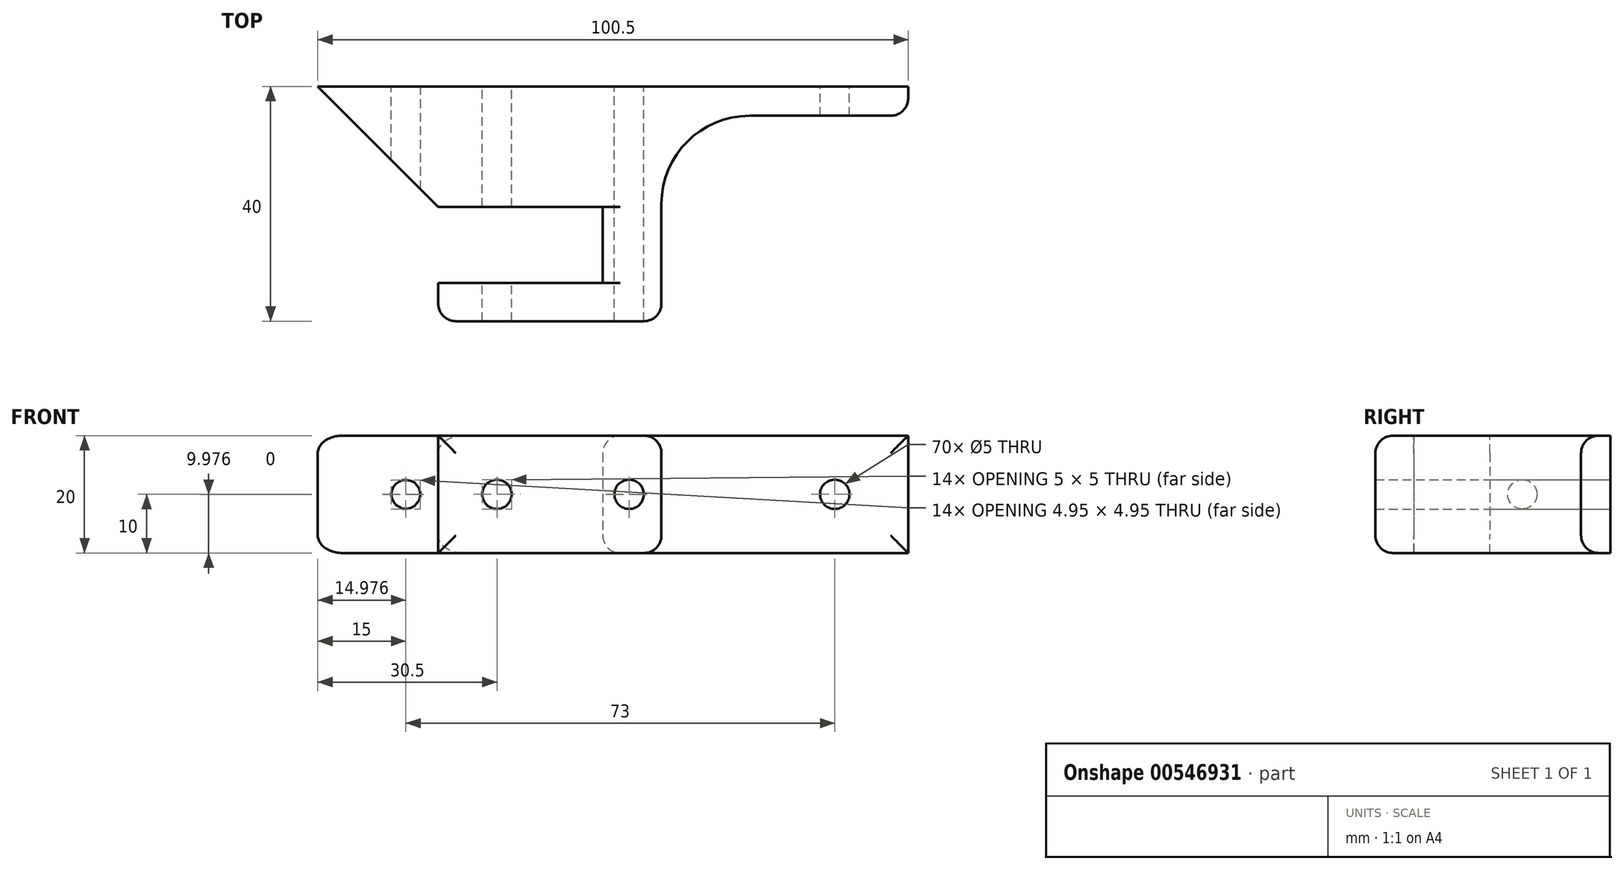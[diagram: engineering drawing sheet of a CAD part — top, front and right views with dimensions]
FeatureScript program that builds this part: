
annotation { "Feature Type Name" : "Feature", "Feature Type Description" : "" }
export const myFeature = defineFeature(function(context is Context, id is Id, definition is map)
    precondition{}
    {
        {
            var Q0;
            Q0=qCreatedBy(makeId("Top.planeOp"),FACE);
            var sketch = newSketch(context, id + "F0", { "sketchPlane" : qUnion([Q0])});
            skLineSegment(sketch, "E0", {"start": v(-20.5, 0) * mm, "end": v(80, 0) * mm});
            skLineSegment(sketch, "E1", {"start": v(0, -40) * mm, "end": v(38, -40) * mm});
            skLineSegment(sketch, "E2", {"start": v(80, -5) * mm, "end": v(80, 0) * mm});
            skLineSegment(sketch, "E3.0", {"start": v(0, -27) * mm, "end": v(38, -27) * mm, "construction": true});
            skLineSegment(sketch, "E4.0", {"start": v(0, -33.5) * mm, "end": v(28, -33.5) * mm});
            skLineSegment(sketch, "E5.0", {"start": v(0, -20.5) * mm, "end": v(28, -20.5) * mm});
            skLineSegment(sketch, "E6.0", {"start": v(28, -20.5) * mm, "end": v(28, -33.5) * mm});
            skLineSegment(sketch, "E7.trimOffspring", {"start": v(0, -33.5) * mm, "end": v(0, -40) * mm});
            skLineSegment(sketch, "E8", {"start": v(0, -20.5) * mm, "end": v(-20.5, 0) * mm});
            skPoint(sketch, "E9.start.orphan", {"position": v(0, 0) * mm});
            skLineSegment(sketch, "E10.0", {"start": v(38, -20) * mm, "end": v(38, -40) * mm});
            skLineSegment(sketch, "E11.0", {"start": v(53, -5) * mm, "end": v(80, -5) * mm});
            skPoint(sketch, "E12.visualSharp", {"position": v(38, -5) * mm});
            skArc(sketch, "E12.filletArc", {"start": v(53, -5) * mm, "mid": v(42.4, -9.4) * mm, "end": v(38, -20) * mm});
            skSolve(sketch);
        }
        {
            var Q0;
            Q0=makeQuery(id+"F0.imprint","IMPRINT",FACE,{"disambiguationData":[TD([[makeQuery(id+"F0.imprint","IMPRINT",EDGE,{"derivedFrom":sQuery(id+"F0.wireOp",EDGE,"E0")}),-1.0]])]});
            extrude(context, id + "F1", {"entities" : qUnion([Q0]), "depth" : 20 * mm, "offsetDistance" : 25 * mm});
        }
        {
            var Q0;
            Q0=qCreatedBy(makeId("Front.planeOp"),FACE);
            var sketch = newSketch(context, id + "F2", { "sketchPlane" : qUnion([Q0])});
            skLineSegment(sketch, "E13", {"start": v(-20.5, 0) * mm, "end": v(80, 0) * mm});
            skLineSegment(sketch, "E14", {"start": v(-20.5, 0) * mm, "end": v(-20.5, 20) * mm});
            skLineSegment(sketch, "E15.0", {"start": v(-20.5, 10) * mm, "end": v(80, 10) * mm, "construction": true});
            skLineSegment(sketch, "E16.0", {"start": v(-5.5, 0) * mm, "end": v(-5.5, 10) * mm, "construction": true});
            skLineSegment(sketch, "E17", {"start": v(0, 0) * mm, "end": v(0, 10) * mm, "construction": true});
            skLineSegment(sketch, "E18.0", {"start": v(10, 0) * mm, "end": v(10, 10) * mm, "construction": true});
            skLineSegment(sketch, "E19.0", {"start": v(32.5, 0) * mm, "end": v(32.5, 10) * mm, "construction": true});
            skLineSegment(sketch, "E20.0", {"start": v(67.5, 0) * mm, "end": v(67.5, 10) * mm, "construction": true});
            skCircle(sketch, "E21", {"center": v(67.5, 10) * mm, "radius": 2.5 * mm});
            skCircle(sketch, "E22", {"center": v(32.5, 10) * mm, "radius": 2.5 * mm});
            skCircle(sketch, "E23", {"center": v(10, 10) * mm, "radius": 2.5 * mm});
            skCircle(sketch, "E24", {"center": v(-5.5, 10) * mm, "radius": 2.5 * mm});
            skSolve(sketch);
        }
        {
            var Q0;
            Q0=makeQuery(id+"F2.imprint","IMPRINT",FACE,{"disambiguationData":[TD([[makeQuery(id+"F2.imprint","IMPRINT",EDGE,{"derivedFrom":sQuery(id+"F2.wireOp",EDGE,"E23")}),1.0]])]});
            var Q1;
            Q1=makeQuery(id+"F2.imprint","IMPRINT",FACE,{"disambiguationData":[TD([[makeQuery(id+"F2.imprint","IMPRINT",EDGE,{"derivedFrom":sQuery(id+"F2.wireOp",EDGE,"E24")}),1.0]])]});
            var Q2;
            Q2=makeQuery(id+"F2.imprint","IMPRINT",FACE,{"disambiguationData":[TD([[makeQuery(id+"F2.imprint","IMPRINT",EDGE,{"derivedFrom":sQuery(id+"F2.wireOp",EDGE,"E22")}),1.0]])]});
            var Q3;
            Q3=makeQuery(id+"F2.imprint","IMPRINT",FACE,{"disambiguationData":[TD([[makeQuery(id+"F2.imprint","IMPRINT",EDGE,{"derivedFrom":sQuery(id+"F2.wireOp",EDGE,"E21")}),1.0]])]});
            extrude(context, id + "F3", {"entities" : qUnion([Q0, Q1, Q2, Q3]), "operationType" : NewBodyOperationType.REMOVE, "depth" : 50 * mm, "offsetDistance" : 25 * mm});
        }
        {
            var Q0;
            Q0=makeQuery(id+"F1.opExtrude","CAP_EDGE",EDGE,{"disambiguationData":[OSD([sQuery(id+"F0.wireOp",EDGE,"E11.0")])],"isStart":false});
            var Q1;
            Q1=makeQuery(id+"F1.opExtrude","CAP_EDGE",EDGE,{"disambiguationData":[OSD([sQuery(id+"F0.wireOp",EDGE,"E1")])],"isStart":false});
            var Q2;
            Q2=makeQuery(id+"F1.opExtrude","SWEPT_EDGE",EDGE,{"disambiguationData":[OSD([sQuery(id+"F0.wireOp",EDGE,"E1"),sQuery(id+"F0.wireOp",EDGE,"E7.trimOffspring")])]});
            var Q3;
            Q3=makeQuery(id+"F1.opExtrude","CAP_EDGE",EDGE,{"disambiguationData":[OSD([sQuery(id+"F0.wireOp",EDGE,"E1")])],"isStart":true});
            var Q4;
            Q4=makeQuery(id+"F1.opExtrude","CAP_EDGE",EDGE,{"disambiguationData":[OSD([sQuery(id+"F0.wireOp",EDGE,"E11.0")])],"isStart":true});
            var Q5;
            Q5=makeQuery(id+"F1.opExtrude","CAP_EDGE",EDGE,{"disambiguationData":[OSD([sQuery(id+"F0.wireOp",EDGE,"E8")])],"isStart":false});
            var Q6;
            Q6=makeQuery(id+"F1.opExtrude","CAP_EDGE",EDGE,{"disambiguationData":[OSD([sQuery(id+"F0.wireOp",EDGE,"E8")])],"isStart":true});
            var Q7;
            Q7=makeQuery(id+"F1.opExtrude","SWEPT_EDGE",EDGE,{"disambiguationData":[OSD([sQuery(id+"F0.wireOp",EDGE,"E2"),sQuery(id+"F0.wireOp",EDGE,"E11.0")])]});
            var Q8;
            Q8=makeQuery(id+"F1.opExtrude","SWEPT_EDGE",EDGE,{"disambiguationData":[OSD([sQuery(id+"F0.wireOp",EDGE,"E1"),sQuery(id+"F0.wireOp",EDGE,"E10.0")])]});
            var Q9;
            Q9=makeQuery(id+"F1.opExtrude","CAP_EDGE",EDGE,{"disambiguationData":[OSD([sQuery(id+"F0.wireOp",EDGE,"E6.0")])],"isStart":false});
            var Q10;
            Q10=makeQuery(id+"F1.opExtrude","CAP_EDGE",EDGE,{"disambiguationData":[OSD([sQuery(id+"F0.wireOp",EDGE,"E6.0")])],"isStart":true});
            fillet(context, id + "F4", {"entities" : qUnion([Q0, Q1, Q2, Q3, Q4, Q5, Q6, Q7, Q8, Q9, Q10]), "radius" : 3 * mm, "tangentPropagation" : true, "allowEdgeOverflow" : false});
        }
    });
